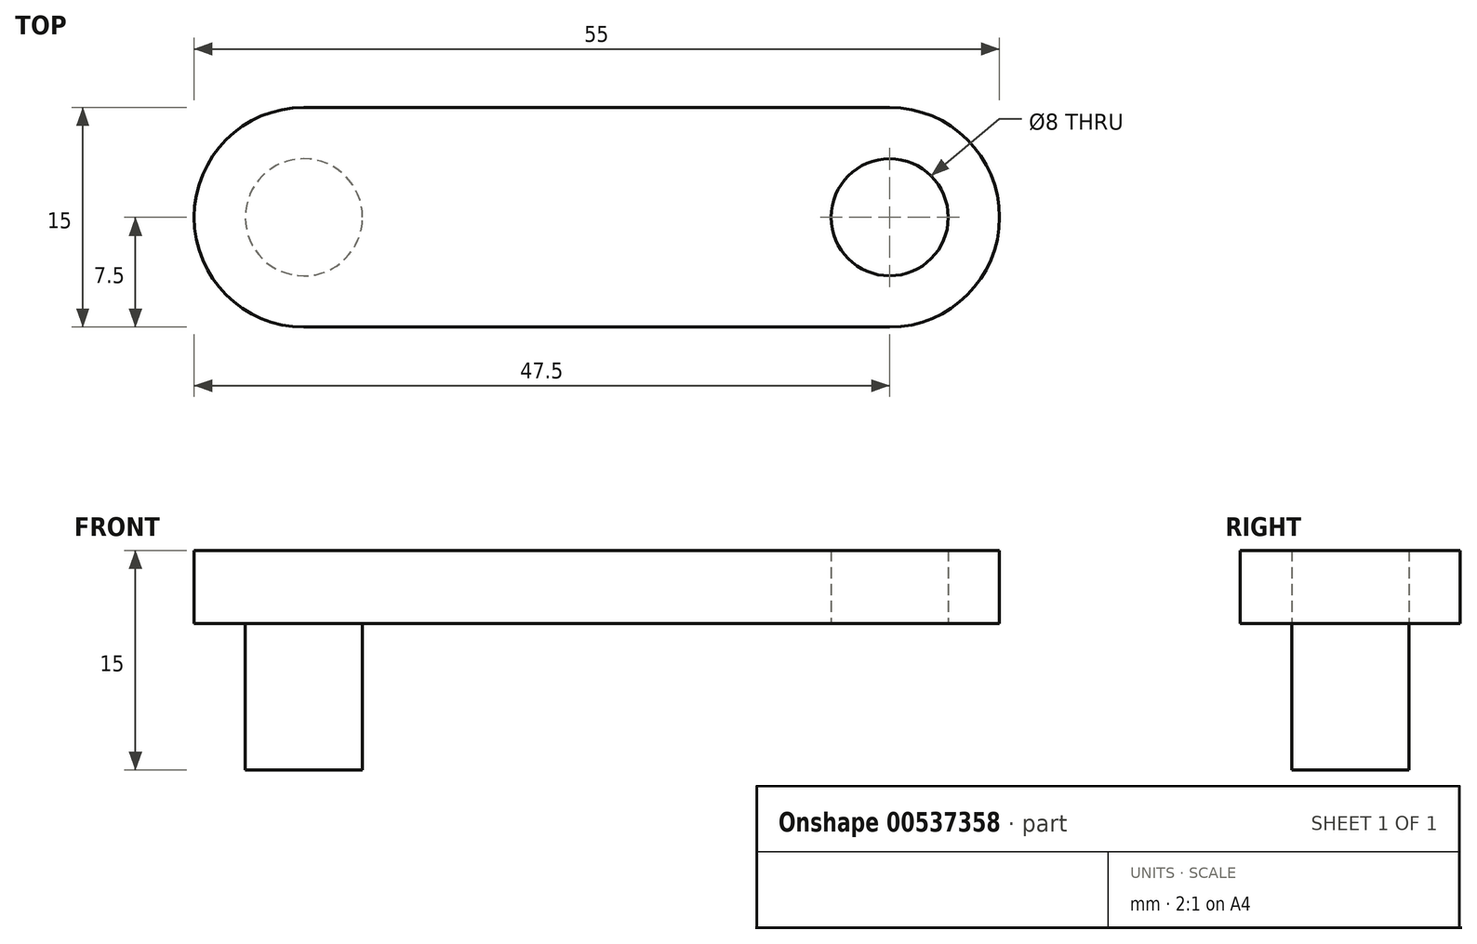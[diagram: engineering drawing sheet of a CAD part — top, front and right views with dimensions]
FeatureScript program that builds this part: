
annotation { "Feature Type Name" : "Feature", "Feature Type Description" : "" }
export const myFeature = defineFeature(function(context is Context, id is Id, definition is map)
    precondition{}
    {
        {
            var Q0;
            Q0=qCreatedBy(makeId("Top.planeOp"),FACE);
            var sketch = newSketch(context, id + "F0", { "sketchPlane" : qUnion([Q0])});
            skLineSegment(sketch, "E0.bottom", {"start": v(20, 7.5) * mm, "end": v(-20, 7.5) * mm});
            skLineSegment(sketch, "E0.top", {"start": v(20, -7.5) * mm, "end": v(-20, -7.5) * mm});
            skPoint(sketch, "E0.middle", {"position": v(0, 0) * mm});
            skArc(sketch, "E1", {"start": v(-20, 7.5) * mm, "mid": v(-27.5, 0) * mm, "end": v(-20, -7.5) * mm});
            skCircle(sketch, "E2", {"center": v(-20, 0) * mm, "radius": 4 * mm});
            skCircle(sketch, "E3", {"center": v(20, 0) * mm, "radius": 4 * mm});
            skArc(sketch, "E4", {"start": v(20, -7.5) * mm, "mid": v(27.5, 0) * mm, "end": v(20, 7.5) * mm});
            skSolve(sketch);
        }
        {
            var Q0;
            Q0=makeQuery(id+"F0.imprint","IMPRINT",FACE,{"disambiguationData":[TD([[makeQuery(id+"F0.imprint","IMPRINT",EDGE,{"derivedFrom":sQuery(id+"F0.wireOp",EDGE,"E0.bottom")}),1.0]])]});
            extrude(context, id + "F1", {"entities" : qUnion([Q0]), "endBound" : BoundingType.SYMMETRIC, "depth" : 5 * mm, "offsetDistance" : 25.4 * mm});
        }
        {
            var Q0;
            Q0=makeQuery(id+"F1.opExtrude","CAP_FACE",FACE,{"disambiguationData":[OSD([sQuery(id+"F0.wireOp",EDGE,"E0.bottom"),sQuery(id+"F0.wireOp",EDGE,"E0.top"),sQuery(id+"F0.wireOp",EDGE,"E1"),sQuery(id+"F0.wireOp",EDGE,"E2"),sQuery(id+"F0.wireOp",EDGE,"E3"),sQuery(id+"F0.wireOp",EDGE,"E4")])],"isStart":false});
            var sketch = newSketch(context, id + "F2", { "sketchPlane" : qUnion([Q0])});
            skCircle(sketch, "E5", {"center": v(-20, 0) * mm, "radius": 4 * mm});
            skSolve(sketch);
        }
        {
            var Q0;
            Q0=qSketchRegion(id+"F2",true);
            extrude(context, id + "F3", {"entities" : qUnion([Q0]), "operationType" : NewBodyOperationType.ADD, "oppositeDirection" : true, "depth" : 15 * mm, "offsetDistance" : 25.4 * mm});
        }
    });
